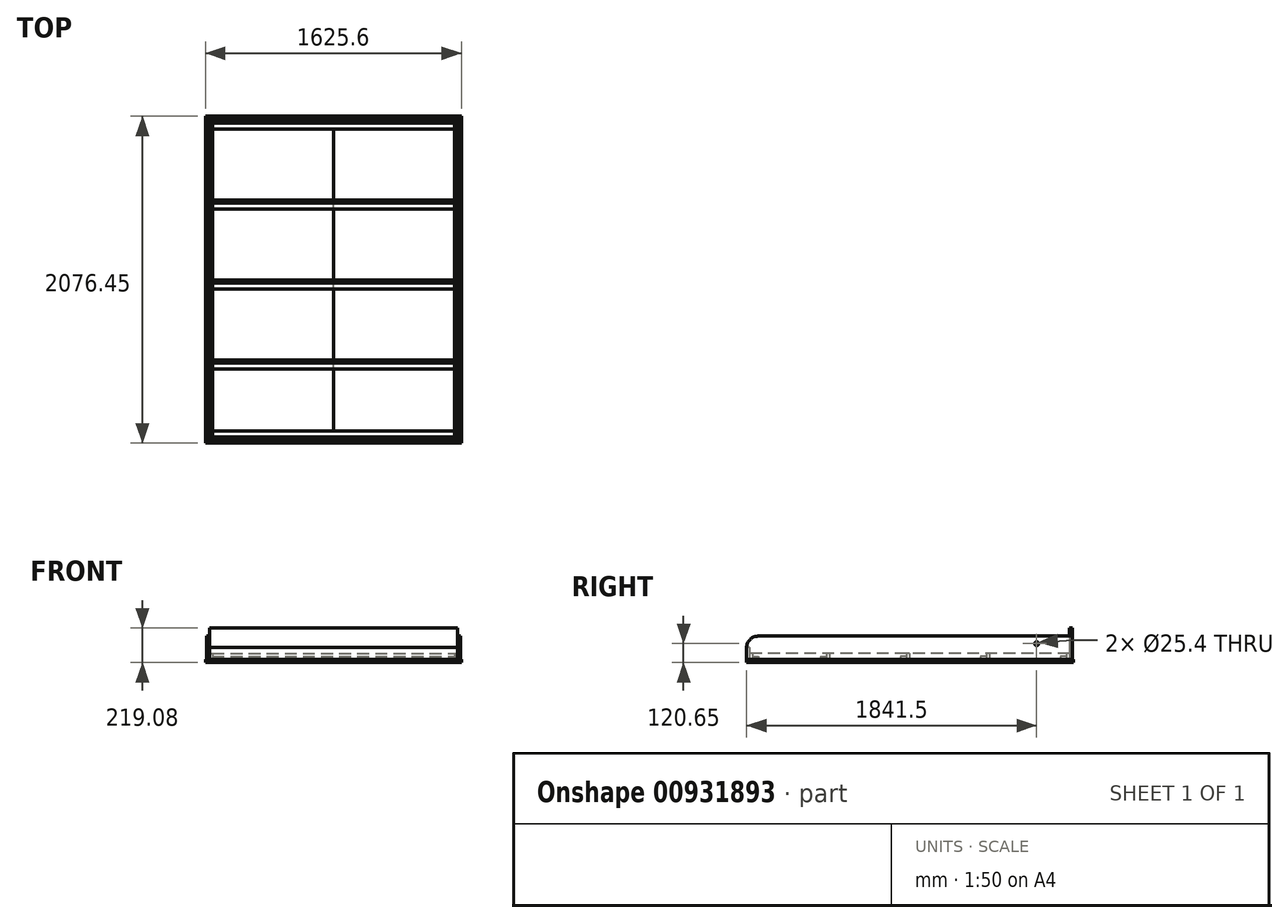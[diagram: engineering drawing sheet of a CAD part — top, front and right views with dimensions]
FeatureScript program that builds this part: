
annotation { "Feature Type Name" : "Feature", "Feature Type Description" : "" }
export const myFeature = defineFeature(function(context is Context, id is Id, definition is map)
    precondition{}
    {
        {
            var Q0;
            Q0=qCreatedBy(makeId("Top.planeOp"),FACE);
            var sketch = newSketch(context, id + "F0", { "sketchPlane" : qUnion([Q0])});
            skLineSegment(sketch, "E0.bottom", {"start": v(0, 0) * mm, "end": v(812.8, 0) * mm});
            skLineSegment(sketch, "E0.top", {"start": v(0, 2076.45) * mm, "end": v(812.8, 2076.45) * mm});
            skLineSegment(sketch, "E0.left", {"start": v(0, 0) * mm, "end": v(0, 2076.45) * mm});
            skLineSegment(sketch, "E0.right", {"start": v(812.8, 0) * mm, "end": v(812.8, 2076.45) * mm});
            skLineSegment(sketch, "E1.bottom", {"start": v(812.8, 2076.45) * mm, "end": v(1625.6, 2076.45) * mm});
            skLineSegment(sketch, "E1.top", {"start": v(812.8, 0) * mm, "end": v(1625.6, 0) * mm});
            skLineSegment(sketch, "E1.left", {"start": v(812.8, 2076.45) * mm, "end": v(812.8, 0) * mm});
            skLineSegment(sketch, "E1.right", {"start": v(1625.6, 2076.45) * mm, "end": v(1625.6, 0) * mm});
            skSolve(sketch);
        }
        {
            var Q0;
            Q0=makeQuery(id+"F0.imprint","IMPRINT",FACE,{"disambiguationData":[TD([[makeQuery(id+"F0.imprint","IMPRINT",EDGE,{"derivedFrom":sQuery(id+"F0.wireOp",EDGE,"E0.bottom")}),1.0]])]});
            extrude(context, id + "F1", {"entities" : qUnion([Q0]), "oppositeDirection" : true, "depth" : 19.05 * mm, "offsetDistance" : 25.4 * mm});
        }
        {
            var Q0;
            Q0=makeQuery(id+"F0.imprint","IMPRINT",FACE,{"disambiguationData":[TD([[makeQuery(id+"F0.imprint","IMPRINT",EDGE,{"derivedFrom":sQuery(id+"F0.wireOp",EDGE,"E1.bottom")}),-1.0]])]});
            extrude(context, id + "F2", {"entities" : qUnion([Q0]), "oppositeDirection" : true, "depth" : 19.05 * mm, "offsetDistance" : 25.4 * mm});
        }
        {
            var Q0;
            Q0=qCreatedBy(makeId("Top.planeOp"),FACE);
            var sketch = newSketch(context, id + "F3", { "sketchPlane" : qUnion([Q0])});
            skLineSegment(sketch, "E2.bottom", {"start": v(44.45, 2051.05) * mm, "end": v(1581.15, 2051.05) * mm});
            skLineSegment(sketch, "E2.top", {"start": v(44.45, 2032) * mm, "end": v(1581.15, 2032) * mm});
            skLineSegment(sketch, "E2.left", {"start": v(44.45, 2051.05) * mm, "end": v(44.45, 2032) * mm});
            skLineSegment(sketch, "E2.right", {"start": v(1581.15, 2051.05) * mm, "end": v(1581.15, 2032) * mm});
            skLineSegment(sketch, "E3.bottom", {"start": v(44.45, 1543.05) * mm, "end": v(1581.15, 1543.05) * mm});
            skLineSegment(sketch, "E3.top", {"start": v(44.45, 1524) * mm, "end": v(1581.15, 1524) * mm});
            skLineSegment(sketch, "E3.left", {"start": v(44.45, 1543.05) * mm, "end": v(44.45, 1524) * mm});
            skLineSegment(sketch, "E3.right", {"start": v(1581.15, 1543.05) * mm, "end": v(1581.15, 1524) * mm});
            skLineSegment(sketch, "E4.bottom", {"start": v(44.45, 1035.05) * mm, "end": v(1581.15, 1035.05) * mm});
            skLineSegment(sketch, "E4.top", {"start": v(44.45, 1016) * mm, "end": v(1581.15, 1016) * mm});
            skLineSegment(sketch, "E4.left", {"start": v(44.45, 1035.05) * mm, "end": v(44.45, 1016) * mm});
            skLineSegment(sketch, "E4.right", {"start": v(1581.15, 1035.05) * mm, "end": v(1581.15, 1016) * mm});
            skLineSegment(sketch, "E5.bottom", {"start": v(44.45, 527.05) * mm, "end": v(1581.15, 527.05) * mm});
            skLineSegment(sketch, "E5.top", {"start": v(44.45, 508) * mm, "end": v(1581.15, 508) * mm});
            skLineSegment(sketch, "E5.left", {"start": v(44.45, 527.05) * mm, "end": v(44.45, 508) * mm});
            skLineSegment(sketch, "E5.right", {"start": v(1581.15, 527.05) * mm, "end": v(1581.15, 508) * mm});
            skLineSegment(sketch, "E6.bottom", {"start": v(44.45, 38.1) * mm, "end": v(1581.15, 38.1) * mm});
            skLineSegment(sketch, "E6.top", {"start": v(44.45, 19.05) * mm, "end": v(1581.15, 19.05) * mm});
            skLineSegment(sketch, "E6.left", {"start": v(44.45, 38.1) * mm, "end": v(44.45, 19.05) * mm});
            skLineSegment(sketch, "E6.right", {"start": v(1581.15, 38.1) * mm, "end": v(1581.15, 19.05) * mm});
            skLineSegment(sketch, "E7", {"start": v(44.45, 2032) * mm, "end": v(44.45, 1993.9) * mm});
            skLineSegment(sketch, "E8", {"start": v(44.45, 1993.9) * mm, "end": v(1581.15, 1993.9) * mm});
            skLineSegment(sketch, "E9", {"start": v(1581.15, 1993.9) * mm, "end": v(1581.15, 2032) * mm});
            skLineSegment(sketch, "E10", {"start": v(44.45, 1524) * mm, "end": v(44.45, 1485.9) * mm});
            skLineSegment(sketch, "E11", {"start": v(44.45, 1485.9) * mm, "end": v(1581.15, 1485.9) * mm});
            skLineSegment(sketch, "E12", {"start": v(1581.15, 1485.9) * mm, "end": v(1581.15, 1524) * mm});
            skLineSegment(sketch, "E13", {"start": v(44.45, 1016) * mm, "end": v(44.45, 977.9) * mm});
            skLineSegment(sketch, "E14", {"start": v(44.45, 977.9) * mm, "end": v(1581.15, 977.9) * mm});
            skLineSegment(sketch, "E15", {"start": v(1581.15, 977.9) * mm, "end": v(1581.15, 1016) * mm});
            skLineSegment(sketch, "E16", {"start": v(44.45, 508) * mm, "end": v(44.45, 469.9) * mm});
            skLineSegment(sketch, "E17", {"start": v(44.45, 469.9) * mm, "end": v(1581.15, 469.9) * mm});
            skLineSegment(sketch, "E18", {"start": v(1581.15, 469.9) * mm, "end": v(1581.15, 508) * mm});
            skLineSegment(sketch, "E19", {"start": v(44.45, 38.1) * mm, "end": v(44.45, 76.2) * mm});
            skLineSegment(sketch, "E20", {"start": v(44.45, 76.2) * mm, "end": v(1581.15, 76.2) * mm});
            skLineSegment(sketch, "E21", {"start": v(1581.15, 76.2) * mm, "end": v(1581.15, 38.1) * mm});
            skLineSegment(sketch, "E22.bottom", {"start": v(25.4, 2051.05) * mm, "end": v(44.45, 2051.05) * mm});
            skLineSegment(sketch, "E22.top", {"start": v(25.4, 19.05) * mm, "end": v(44.45, 19.05) * mm});
            skLineSegment(sketch, "E22.left", {"start": v(25.4, 2051.05) * mm, "end": v(25.4, 19.05) * mm});
            skLineSegment(sketch, "E22.right", {"start": v(44.45, 2051.05) * mm, "end": v(44.45, 19.05) * mm});
            skLineSegment(sketch, "E23.bottom", {"start": v(1581.15, 2051.05) * mm, "end": v(1600.2, 2051.05) * mm});
            skLineSegment(sketch, "E23.top", {"start": v(1581.15, 19.05) * mm, "end": v(1600.2, 19.05) * mm});
            skLineSegment(sketch, "E23.left", {"start": v(1581.15, 2051.05) * mm, "end": v(1581.15, 19.05) * mm});
            skLineSegment(sketch, "E23.right", {"start": v(1600.2, 2051.05) * mm, "end": v(1600.2, 19.05) * mm});
            skLineSegment(sketch, "E24.bottom", {"start": v(6.35, 2070.1) * mm, "end": v(25.4, 2070.1) * mm});
            skLineSegment(sketch, "E24.top", {"start": v(6.35, 0) * mm, "end": v(25.4, 0) * mm});
            skLineSegment(sketch, "E24.left", {"start": v(6.35, 2070.1) * mm, "end": v(6.35, 0) * mm});
            skLineSegment(sketch, "E24.right", {"start": v(25.4, 2070.1) * mm, "end": v(25.4, 0) * mm});
            skLineSegment(sketch, "E25.bottom", {"start": v(1600.2, 2070.1) * mm, "end": v(1619.25, 2070.1) * mm});
            skLineSegment(sketch, "E25.top", {"start": v(1600.2, 0) * mm, "end": v(1619.25, 0) * mm});
            skLineSegment(sketch, "E25.left", {"start": v(1600.2, 2070.1) * mm, "end": v(1600.2, 0) * mm});
            skLineSegment(sketch, "E25.right", {"start": v(1619.25, 2070.1) * mm, "end": v(1619.25, 0) * mm});
            skLineSegment(sketch, "E26.bottom", {"start": v(25.4, 19.05) * mm, "end": v(1600.2, 19.05) * mm});
            skLineSegment(sketch, "E26.top", {"start": v(25.4, 0) * mm, "end": v(1600.2, 0) * mm});
            skLineSegment(sketch, "E26.left", {"start": v(25.4, 19.05) * mm, "end": v(25.4, 0) * mm});
            skLineSegment(sketch, "E26.right", {"start": v(1600.2, 19.05) * mm, "end": v(1600.2, 0) * mm});
            skLineSegment(sketch, "E27.bottom", {"start": v(25.4, 2070.1) * mm, "end": v(1600.2, 2070.1) * mm});
            skLineSegment(sketch, "E27.top", {"start": v(25.4, 2051.05) * mm, "end": v(1600.2, 2051.05) * mm});
            skLineSegment(sketch, "E27.left", {"start": v(25.4, 2070.1) * mm, "end": v(25.4, 2051.05) * mm});
            skLineSegment(sketch, "E27.right", {"start": v(1600.2, 2070.1) * mm, "end": v(1600.2, 2051.05) * mm});
            skSolve(sketch);
        }
        {
            var Q0;
            Q0=makeQuery(id+"F3.imprint","IMPRINT",FACE,{"disambiguationData":[TD([[makeQuery(id+"F3.imprint","IMPRINT",EDGE,{"derivedFrom":sQuery(id+"F3.wireOp",EDGE,"E2.top")}),-1.0]])]});
            var Q1;
            Q1=makeQuery(id+"F3.imprint","IMPRINT",FACE,{"disambiguationData":[TD([[makeQuery(id+"F3.imprint","IMPRINT",EDGE,{"derivedFrom":sQuery(id+"F3.wireOp",EDGE,"E3.top")}),-1.0]])]});
            var Q2;
            Q2=makeQuery(id+"F3.imprint","IMPRINT",FACE,{"disambiguationData":[TD([[makeQuery(id+"F3.imprint","IMPRINT",EDGE,{"derivedFrom":sQuery(id+"F3.wireOp",EDGE,"E4.top")}),-1.0]])]});
            var Q3;
            Q3=makeQuery(id+"F3.imprint","IMPRINT",FACE,{"disambiguationData":[TD([[makeQuery(id+"F3.imprint","IMPRINT",EDGE,{"derivedFrom":sQuery(id+"F3.wireOp",EDGE,"E5.top")}),-1.0]])]});
            var Q4;
            Q4=makeQuery(id+"F3.imprint","IMPRINT",FACE,{"disambiguationData":[TD([[makeQuery(id+"F3.imprint","IMPRINT",EDGE,{"derivedFrom":sQuery(id+"F3.wireOp",EDGE,"E6.bottom")}),1.0]])]});
            extrude(context, id + "F4", {"entities" : qUnion([Q0, Q1, Q2, Q3, Q4]), "depth" : 19.05 * mm, "offsetDistance" : 25.4 * mm});
        }
        {
            var Q0;
            Q0=makeQuery(id+"F3.imprint","IMPRINT",FACE,{"disambiguationData":[TD([[makeQuery(id+"F3.imprint","IMPRINT",EDGE,{"derivedFrom":sQuery(id+"F3.wireOp",EDGE,"E2.bottom")}),-1.0]])]});
            var Q1;
            Q1=makeQuery(id+"F3.imprint","IMPRINT",FACE,{"disambiguationData":[TD([[makeQuery(id+"F3.imprint","IMPRINT",EDGE,{"derivedFrom":sQuery(id+"F3.wireOp",EDGE,"E3.bottom")}),-1.0]])]});
            var Q2;
            Q2=makeQuery(id+"F3.imprint","IMPRINT",FACE,{"disambiguationData":[TD([[makeQuery(id+"F3.imprint","IMPRINT",EDGE,{"derivedFrom":sQuery(id+"F3.wireOp",EDGE,"E4.bottom")}),-1.0]])]});
            var Q3;
            Q3=makeQuery(id+"F3.imprint","IMPRINT",FACE,{"disambiguationData":[TD([[makeQuery(id+"F3.imprint","IMPRINT",EDGE,{"derivedFrom":sQuery(id+"F3.wireOp",EDGE,"E5.bottom")}),-1.0]])]});
            var Q4;
            Q4=makeQuery(id+"F3.imprint","IMPRINT",FACE,{"disambiguationData":[TD([[makeQuery(id+"F3.imprint","IMPRINT",EDGE,{"derivedFrom":sQuery(id+"F3.wireOp",EDGE,"E6.bottom")}),-1.0]])]});
            extrude(context, id + "F5", {"entities" : qUnion([Q0, Q1, Q2, Q3, Q4]), "depth" : 38.1 * mm, "offsetDistance" : 25.4 * mm});
        }
        {
            var Q0;
            Q0=makeQuery(id+"F3.imprint","IMPRINT",FACE,{"disambiguationData":[TD([[makeQuery(id+"F3.imprint","IMPRINT",EDGE,{"derivedFrom":sQuery(id+"F3.wireOp",EDGE,"E2.left")}),-1.0]])]});
            var Q1;
            Q1=makeQuery(id+"F3.imprint","IMPRINT",FACE,{"disambiguationData":[TD([[makeQuery(id+"F3.imprint","IMPRINT",EDGE,{"derivedFrom":sQuery(id+"F3.wireOp",EDGE,"E2.right")}),1.0]])]});
            extrude(context, id + "F6", {"entities" : qUnion([Q0, Q1]), "depth" : 38.1 * mm, "offsetDistance" : 25.4 * mm});
        }
        {
            var Q0;
            Q0=makeQuery(id+"F3.imprint","IMPRINT",FACE,{"disambiguationData":[TD([[makeQuery(id+"F3.imprint","IMPRINT",EDGE,{"derivedFrom":sQuery(id+"F3.wireOp",EDGE,"E6.top")}),-1.0]])]});
            extrude(context, id + "F7", {"entities" : qUnion([Q0]), "depth" : 76.2 * mm, "offsetDistance" : 25.4 * mm});
        }
        {
            var Q0;
            {var subQ2=sQuery(id+"F3.wireOp",EDGE,"E22.left");Q0=makeQuery(id+"F3.imprint","IMPRINT",FACE,{"disambiguationData":[TD([[makeQuery(id+"F3.imprint","IMPRINT",EDGE,{"derivedFrom":subQ2}),-1.0]])]});}
            var Q1;
            {var subQ1=sQuery(id+"F3.wireOp",EDGE,"E23.right");Q1=makeQuery(id+"F3.imprint","IMPRINT",FACE,{"disambiguationData":[TD([[makeQuery(id+"F3.imprint","IMPRINT",EDGE,{"derivedFrom":subQ1}),1.0]])]});}
            extrude(context, id + "F8", {"entities" : qUnion([Q0, Q1]), "depth" : 149.22 * mm, "offsetDistance" : 25.4 * mm});
        }
        {
            var Q0;
            Q0=makeQuery(id+"F3.imprint","IMPRINT",FACE,{"disambiguationData":[TD([[makeQuery(id+"F3.imprint","IMPRINT",EDGE,{"derivedFrom":sQuery(id+"F3.wireOp",EDGE,"E2.bottom")}),1.0]])]});
            extrude(context, id + "F9", {"entities" : qUnion([Q0]), "depth" : 200.02 * mm, "offsetDistance" : 25.4 * mm});
        }
        {
            var Q0;
            Q0=makeQuery(id+"F8.opExtrude","CAP_EDGE",EDGE,{"disambiguationData":[OSD([sQuery(id+"F3.wireOp",EDGE,"E24.top")])],"isStart":false});
            var Q1;
            Q1=makeQuery(id+"F8.opExtrude","CAP_EDGE",EDGE,{"disambiguationData":[OSD([sQuery(id+"F3.wireOp",EDGE,"E25.top")])],"isStart":false});
            fillet(context, id + "F10", {"entities" : qUnion([Q0, Q1]), "radius" : 73.02 * mm, "tangentPropagation" : true, "allowEdgeOverflow" : false});
        }
        {
            var Q0;
            Q0=makeQuery(id+"F8.opExtrude","SWEPT_FACE",FACE,{"disambiguationData":[OSD([sQuery(id+"F3.wireOp",EDGE,"E24.left")])]});
            var sketch = newSketch(context, id + "F11", { "sketchPlane" : qUnion([Q0])});
            skCircle(sketch, "E28", {"center": v(-1841.5, 101.6) * mm, "radius": 12.7 * mm});
            skSolve(sketch);
        }
        {
            var Q0;
            Q0 = qSketchRegion(id + "F11", true);
            extrude(context, id + "F12", {"entities" : qUnion([Q0]), "operationType" : NewBodyOperationType.REMOVE, "endBound" : BoundingType.THROUGH_ALL, "oppositeDirection" : true, "depth" : 25.4 * mm, "offsetDistance" : 25.4 * mm});
        }
        {
            var Q0;
            Q0=qCreatedBy(makeId("Top.planeOp"),FACE);
            cPlane(context, id + "F13", {"entities" : qUnion([Q0]), "cplaneType" : CPlaneType.OFFSET, "offset" : 76.2 * mm, "oppositeDirection" : true, "width" : 152.4 * mm, "height" : 152.4 * mm});
        }
    });
